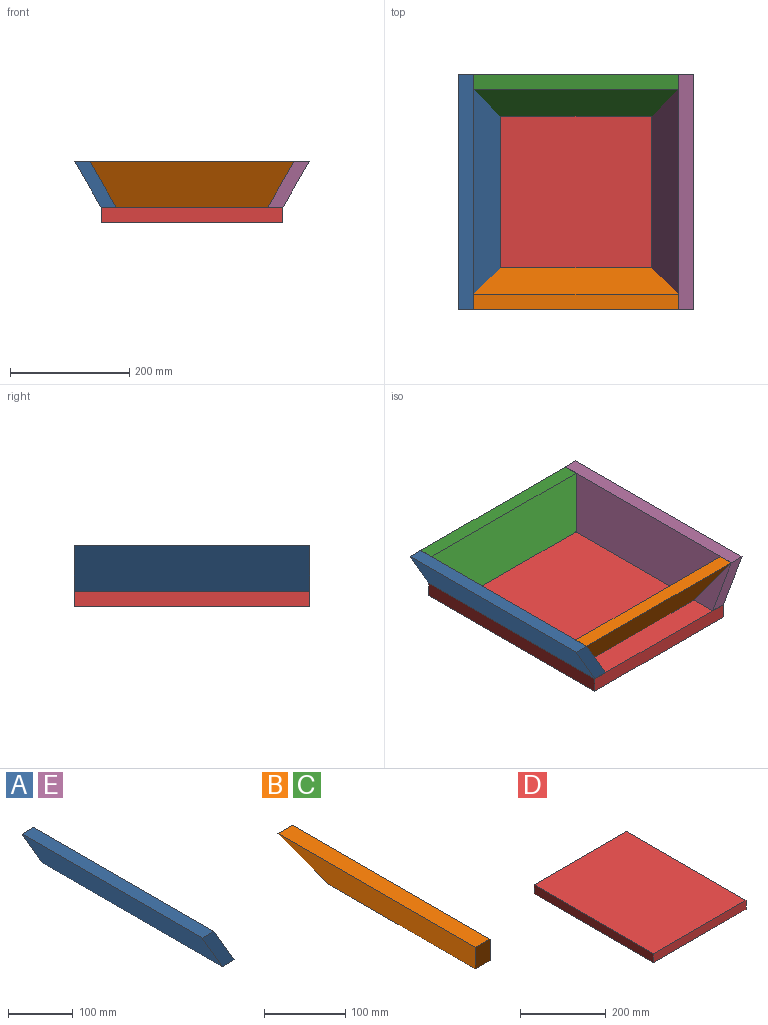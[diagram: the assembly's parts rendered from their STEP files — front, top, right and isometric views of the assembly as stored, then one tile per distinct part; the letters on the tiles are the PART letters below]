
ASSEMBLY  parts=5 mates=4
PART A: 6 faces, bbox 69.4x393.7x76.2 mm
  f0: plane 393.7x76.2mm, normal (-0.87,0,-0.5), area 34640.9mm2, adj f1,f3,f4,f5
  f1: plane 393.7x25.4mm, normal (0,0,-1), area 10000mm2, adj f0,f2,f4,f5
  f2: plane 393.7x76.2mm, normal (0.87,0,0.5), area 34640.9mm2, adj f1,f3,f4,f5
  f3: plane 393.7x25.4mm, normal (0,0,1), area 10000mm2, adj f0,f2,f4,f5
  f4: plane 76.2x69.39mm, normal (0,-1,0), area 1935.5mm2, adj f0,f1,f2,f3
  f5: plane 76.2x69.39mm, normal (0,1,0), area 1935.5mm2, adj f0,f1,f2,f3
PART B: 6 faces, bbox 69.4x342.9x76.2 mm
  f0: plane 254.91x25.4mm, normal (0,0,-1), area 6474.8mm2, adj f1,f2,f4,f5
  f1: plane 342.9x76.2mm, normal (-0.87,0,-0.5), area 26300.2mm2, adj f0,f3,f4,f5
  f2: plane 342.9x76.2mm, normal (0.87,0,0.5), area 26300.2mm2, adj f0,f3,f4,f5
  f3: plane 342.9x25.4mm, normal (0,0,1), area 8709.7mm2, adj f1,f2,f4,f5
  f4: plane 76.2x69.39mm, normal (0,-0.87,-0.5), area 2234.9mm2, adj f0,f1,f2,f3
  f5: plane 76.2x69.39mm, normal (0,0.87,-0.5), area 2234.9mm2, adj f0,f1,f2,f3
PART C: same geometry as B
PART D: 6 faces, bbox 304.8x393.7x25.4 mm
  f0: plane 304.8x25.4mm, normal (0,1,0), area 7741.9mm2, adj f1,f3,f4,f5
  f1: plane 393.7x25.4mm, normal (-1,0,0), area 10000mm2, adj f0,f2,f4,f5
  f2: plane 304.8x25.4mm, normal (0,-1,0), area 7741.9mm2, adj f1,f3,f4,f5
  f3: plane 393.7x25.4mm, normal (1,0,0), area 10000mm2, adj f0,f2,f4,f5
  f4: plane 393.7x304.8mm, normal (0,0,1), area 119999.8mm2, adj f0,f1,f2,f3
  f5: plane 393.7x304.8mm, normal (0,0,-1), area 119999.8mm2, adj f0,f1,f2,f3
PART E: same geometry as A
PLACE A t=(-152.4,0,25.4)mm
PLACE B rot(axis=(0,0,1),90deg) t=(0,-152.4,25.4)mm
PLACE C rot(axis=(0,0,-1),90deg) t=(0,152.4,25.4)mm
PLACE D at identity
PLACE E rot(axis=(0,0,1),180deg) t=(152.4,0,25.4)mm
MATE fastened D.f4 <-> E.f1  axis (0,0,1) through (152.4,0,25.4)mm
MATE fastened D.f4 <-> A.f1  axis (0,0,1) through (-152.4,0,25.4)mm
MATE fastened C.f0 <-> D.f4  axis (0,0,-1) through (0,127,25.4)mm
MATE fastened B.f0 <-> D.f4  axis (0,0,-1) through (0,-127,25.4)mm
